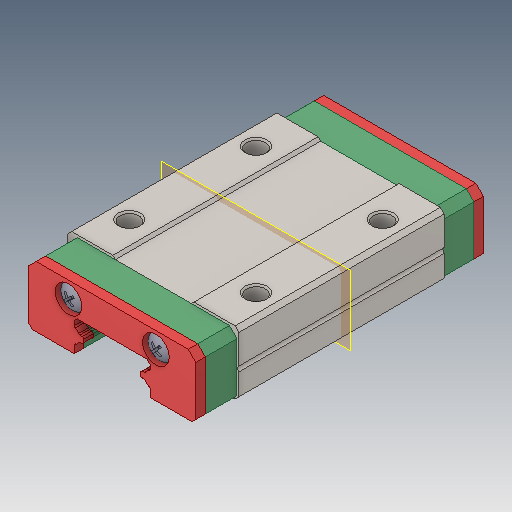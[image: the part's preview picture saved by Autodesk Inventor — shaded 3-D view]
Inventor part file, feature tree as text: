
AUTODESK INVENTOR PART (.ipt)
format: ipt  version: 2019.4 (Build 234330000, 330)  size: 473,088 bytes
history: imported  units: mm
features: other x9, plane x1, imported_body x1
ambient origin geometry x8: Origin, YZ Plane, XZ Plane, XY Plane, X Axis, Y Axis, Z Axis, Center Point
bodies: Solid1 (imported_parasolid), Solid2 (imported_parasolid), Solid3 (imported_parasolid), Solid4 (imported_parasolid), Solid5 (imported_parasolid), Solid6 (imported_parasolid), Solid7 (imported_parasolid), Solid8 (imported_parasolid), Solid9 (imported_parasolid)
feature tree (11):
  plane  "Work Plane1"
  other  "MID BODY, MGN 12H, LINEAR GUIDE BLOCK-1-solid1"
  other  "MID BODY, MGN 12H, LINEAR GUIDE BLOCK-1-solid2"
  other  "MID BODY, MGN 12H, LINEAR GUIDE BLOCK-1-solid3"
  other  "MID BODY, MGN 12H, LINEAR GUIDE BLOCK-1-solid4"
  other  "MID BODY, MGN 12H, LINEAR GUIDE BLOCK-1-solid5"
  other  "SCREW HEAD, MGN 12H, LINEAR GUIDE BLOCK-1-solid1"
  other  "SCREW HEAD, MGN 12H, LINEAR GUIDE BLOCK-2-solid1"
  other  "SCREW HEAD, MGN 12H, LINEAR GUIDE BLOCK-3-solid1"
  other  "SCREW HEAD, MGN 12H, LINEAR GUIDE BLOCK-4-solid1"
  imported_body  NMx_Import_Brep_tag  [imported B-rep: ~50 faces, bbox_mm=[19.044812, 8.226555, 32.4]]
